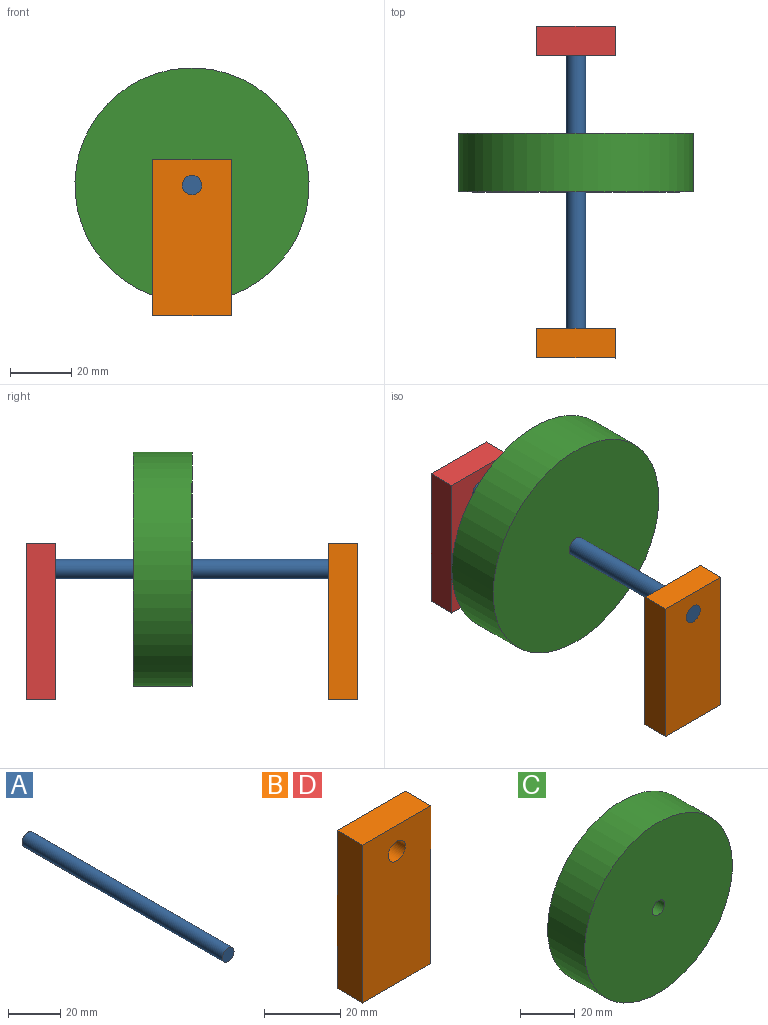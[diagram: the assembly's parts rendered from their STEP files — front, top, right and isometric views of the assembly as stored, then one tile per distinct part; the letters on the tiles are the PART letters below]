
ASSEMBLY  parts=4 mates=8
PART A: 3 faces, bbox 6.4x108x6.4 mm
  f0: cylinder r=3.17mm len=107.95mm, axis (0,1,0), area 2153.5mm2, adj f1,f2
  f1: plane 6.35x6.35mm, normal (0,-1,0), area 31.7mm2, adj f0
  f2: plane 6.35x6.35mm, normal (0,1,0), area 31.7mm2, adj f0
PART B: 7 faces, bbox 25.4x9.5x50.8 mm
  f0: plane 25.4x9.53mm, normal (0,0,1), area 241.9mm2, adj f1,f4,f5,f6
  f1: plane 50.8x9.53mm, normal (-1,0,0), area 483.9mm2, adj f0,f2,f5,f6
  f2: plane 25.4x9.53mm, normal (0,0,-1), area 241.9mm2, adj f1,f4,f5,f6
  f3: cylinder r=3.17mm len=9.53mm, axis (0,1,0), area 190mm2, adj f5,f6
  f4: plane 50.8x9.53mm, normal (1,0,0), area 483.9mm2, adj f0,f2,f5,f6
  f5: plane 50.8x25.4mm, normal (0,-1,0), area 1258.7mm2, adj f0,f1,f2,f3,f4
  f6: plane 50.8x25.4mm, normal (0,1,0), area 1258.7mm2, adj f0,f1,f2,f3,f4
PART C: 4 faces, bbox 76.2x19.1x76.2 mm
  f0: cylinder r=3.17mm len=19.05mm, axis (0,1,0), area 380mm2, adj f2,f3
  f1: cylinder r=38.1mm len=76.2mm, axis (0,1,0), area 4560.4mm2, adj f2,f3
  f2: plane 76.2x76.2mm, normal (0,-1,0), area 4528.7mm2, adj f0,f1
  f3: plane 76.2x76.2mm, normal (0,1,0), area 4528.7mm2, adj f0,f1
PART D: same geometry as B
PLACE A rot(axis=(0,1,0),0deg) t=(169.51,138.9,30.96)mm
PLACE B rot(axis=(0,1,0),0deg) t=(172.28,40.47,43.5)mm
PLACE C t=(169.51,103.97,30.96)mm
PLACE D t=(172.28,138.9,43.5)mm
MATE cylindrical A.f0 <-> C.f1  axis (0,1,0) through (169.51,84.92,30.96)mm
MATE parallel D.f3 <-> A.f0  axis (0,1,0) through (169.51,138.9,30.96)mm
MATE fastened D.f3 <-> A.f0  axis (0,1,0) through (169.51,138.9,30.96)mm
MATE parallel D.f5 <-> A.f0  axis (0,-1,0) through (169.51,129.37,13.36)mm
MATE parallel B.f6 <-> A.f0  axis (0,1,0) through (169.51,40.47,-11.61)mm
MATE parallel A.f0 <-> D.f5  axis (0,1,0) through (169.51,138.9,30.96)mm
MATE fastened A.f0 <-> B.f3  axis (0,-1,0) through (169.51,30.95,30.96)mm
MATE fastened C.f0 <-> A.f0  axis (0,-1,0) through (169.51,84.92,30.96)mm
